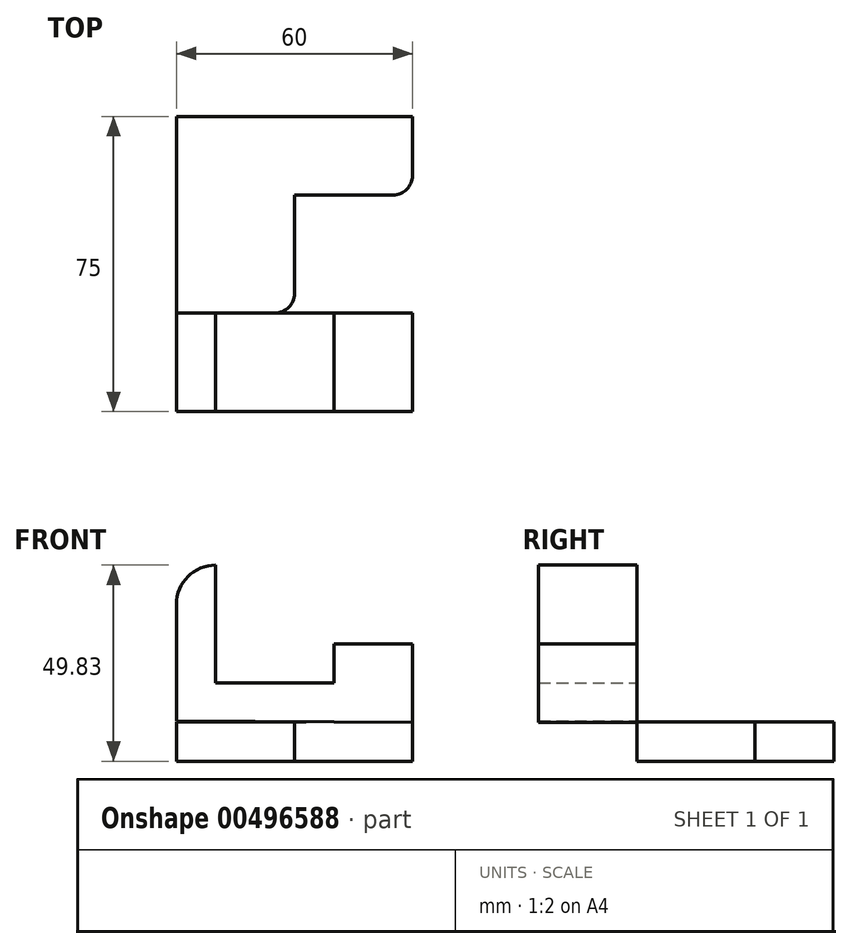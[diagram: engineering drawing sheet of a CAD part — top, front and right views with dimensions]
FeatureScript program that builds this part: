
annotation { "Feature Type Name" : "Feature", "Feature Type Description" : "" }
export const myFeature = defineFeature(function(context is Context, id is Id, definition is map)
    precondition{}
    {
        {
            var Q0;
            Q0=qCreatedBy(makeId("Top.planeOp"),FACE);
            var sketch = newSketch(context, id + "F0", { "sketchPlane" : qUnion([Q0])});
            skLineSegment(sketch, "E0", {"start": v(0, 0) * mm, "end": v(0, 50) * mm});
            skLineSegment(sketch, "E1", {"start": v(0, 50) * mm, "end": v(60, 50) * mm});
            skLineSegment(sketch, "E2", {"start": v(60, 50) * mm, "end": v(60, 35) * mm});
            skLineSegment(sketch, "E3", {"start": v(55, 30) * mm, "end": v(30, 30) * mm});
            skLineSegment(sketch, "E4", {"start": v(30, 30) * mm, "end": v(30, 5) * mm});
            skLineSegment(sketch, "E5", {"start": v(25, 0) * mm, "end": v(0, 0) * mm});
            skPoint(sketch, "E6.visualSharp", {"position": v(60, 30) * mm});
            skArc(sketch, "E6.filletArc", {"start": v(55, 30) * mm, "mid": v(58.54, 31.46) * mm, "end": v(60, 35) * mm});
            skPoint(sketch, "E7.visualSharp", {"position": v(30, 0) * mm});
            skArc(sketch, "E7.filletArc", {"start": v(25, 0) * mm, "mid": v(28.54, 1.46) * mm, "end": v(30, 5) * mm});
            skSolve(sketch);
        }
        {
            var Q0;
            Q0 = qSketchRegion(id + "F0", true);
            extrude(context, id + "F1", {"entities" : qUnion([Q0]), "depth" : 10 * mm});
        }
        {
            var Q0;
            Q0=qCreatedBy(makeId("Front.planeOp"),FACE);
            var sketch = newSketch(context, id + "F2", { "sketchPlane" : qUnion([Q0])});
            skPoint(sketch, "E8.start.orphan", {"position": v(0, 12.63) * mm});
            skLineSegment(sketch, "E9", {"start": v(60, 9.83) * mm, "end": v(60, 29.83) * mm});
            skLineSegment(sketch, "E10", {"start": v(60, 29.83) * mm, "end": v(40, 29.83) * mm});
            skLineSegment(sketch, "E11", {"start": v(40, 29.83) * mm, "end": v(40, 19.83) * mm});
            skLineSegment(sketch, "E12", {"start": v(40, 19.83) * mm, "end": v(10, 19.83) * mm});
            skLineSegment(sketch, "E13", {"start": v(10, 19.83) * mm, "end": v(10, 49.83) * mm});
            skLineSegment(sketch, "E14", {"start": v(10, 49.83) * mm, "end": v(10, 49.83) * mm});
            skLineSegment(sketch, "E15", {"start": v(0, 39.83) * mm, "end": v(0, 10.2) * mm});
            skPoint(sketch, "E16.visualSharp", {"position": v(0, 49.83) * mm});
            skArc(sketch, "E16.filletArc", {"start": v(10, 49.83) * mm, "mid": v(2.93, 46.9) * mm, "end": v(0, 39.83) * mm});
            skLineSegment(sketch, "E17", {"start": v(60, 9.83) * mm, "end": v(0, 10.2) * mm});
            skSolve(sketch);
        }
        {
            var Q0;
            Q0 = qSketchRegion(id + "F2", true);
            extrude(context, id + "F3", {"entities" : qUnion([Q0]), "depth" : 25 * mm, "offsetDistance" : 25 * mm});
        }
        {
            var Q0;
            Q0 = qSketchRegion(id + "F2", true);
            extrude(context, id + "F4", {"entities" : qUnion([Q0]), "operationType" : NewBodyOperationType.ADD, "depth" : 25 * mm, "offsetDistance" : 25 * mm});
        }
    });
